# Revit family: Trane_TVR_Indoor_Floor standing_4TVS0007(09)EF000AA(2nd DC)
name_source: partatom
category: Equipamento mecânico
units: mm (PartAtom-declared; Revit-internal decimal feet)

## family parameters
Com base no plano de trabalho = Não
Compartilhado = Não
Corte com vazios quando carregada = Não
Cota do conector redondo = Utilizar diâmetro
Número OmniClass = 23.75.00.00
Ponto de cálculo do ambiente = Não
Sempre na vertical = Sim
Tipo de parte = Normal
Título OmniClass = Climate Control (HVAC)

## types (2) — shared parameters
Condensation = air
Depth = 212  [stored 0.695538 ft]
Descrição = High efficiency air cooled
Drain pipe = 16  [stored 0.0524934 ft]
Fabricante = Trane
Gas = R410a
Gas pipe = 12.7  [stored 0.0416667 ft]
Height = 545  [stored 1.78806 ft]
Installation = Indoor installation
Liquid pipe = 6.35  [stored 0.0208333 ft]
Machine material = grilles：ABS/HIPS
Maximum Fuse Amps = 15.000 A
Net Weight = 21.00 kg
Power supply = 220-240V ~50/60Hz
Series = TVR ULTRA
URL = https://www.trane.com
Width = 840  [stored 2.75591 ft]

## per-type parameters (varying)
| type | Air Flow | Cooling Capacity | Cooling Power Input | Heating Capacity | Heating Power Input | Minimum Circuit Amps |
| 4TVS0007EF000AA | 530/504/478/456/439/418/400 | 2 kW | 40 W | 2 kW | 40 W | 0.490 A |
| 4TVS0009EF000AA | 569/540/515/485/462/443/421m3/h | 3 kW | 45 W | 3 kW | 45 W | 0.550 A |

note: column(s) folded — value = type name in every type: Modelo

note: [stored X ft] marks values corroborated as IEEE doubles in the binary element streams (Revit-internal decimal feet)

## geometry (parser evidence)
native form markers: Blend x2, Sweep x5
no freeform markers — native parametric forms only
